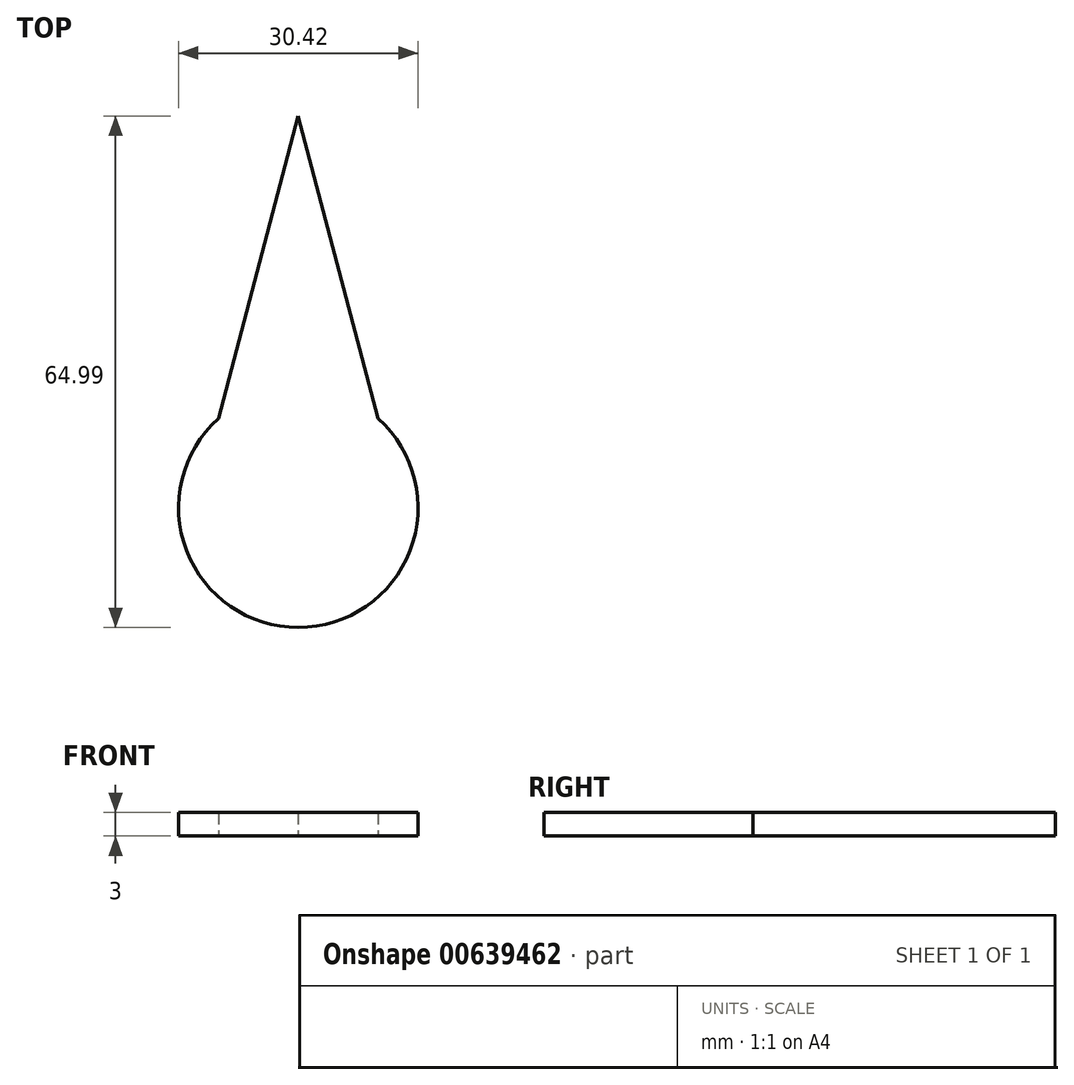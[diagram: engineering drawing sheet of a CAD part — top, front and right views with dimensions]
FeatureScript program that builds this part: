
annotation { "Feature Type Name" : "Feature", "Feature Type Description" : "" }
export const myFeature = defineFeature(function(context is Context, id is Id, definition is map)
    precondition{}
    {
        {
            var Q0;
            Q0=qCreatedBy(makeId("Top.planeOp"),FACE);
            var sketch = newSketch(context, id + "F0", { "sketchPlane" : qUnion([Q0])});
            skCircle(sketch, "E0", {"center": v(0, 0) * mm, "radius": 15.2 * mm});
            skLineSegment(sketch, "E1", {"start": v(-10.15, 11.33) * mm, "end": v(0, 49.78) * mm});
            skLineSegment(sketch, "E2", {"start": v(0, 49.78) * mm, "end": v(10.15, 11.33) * mm});
            skSolve(sketch);
        }
        {
            var Q0;
            {var subQ0=sQuery(id+"F0.wireOp",EDGE,"E0");var subQ1=makeQuery(id+"F0.imprint","INTERSECT",VERTEX,{"derivedFrom":[subQ0,sQuery(id+"F0.wireOp",EDGE,"E1")]});Q0=makeQuery(id+"F0.imprint","IMPRINT",FACE,{"disambiguationData":[TD([[makeQuery(id+"F0.imprint","IMPRINT",EDGE,{"disambiguationData":[TD([[subQ1,1.0]])],"derivedFrom":subQ0}),1.0]])]});}
            var Q1;
            {var subQ0=sQuery(id+"F0.wireOp",EDGE,"E1");Q1=makeQuery(id+"F0.imprint","IMPRINT",FACE,{"disambiguationData":[TD([[makeQuery(id+"F0.imprint","IMPRINT",EDGE,{"derivedFrom":subQ0}),-1.0]])]});}
            extrude(context, id + "F1", {"entities" : qUnion([Q0, Q1]), "depth" : 3 * mm, "offsetDistance" : 25.4 * mm});
        }
    });
